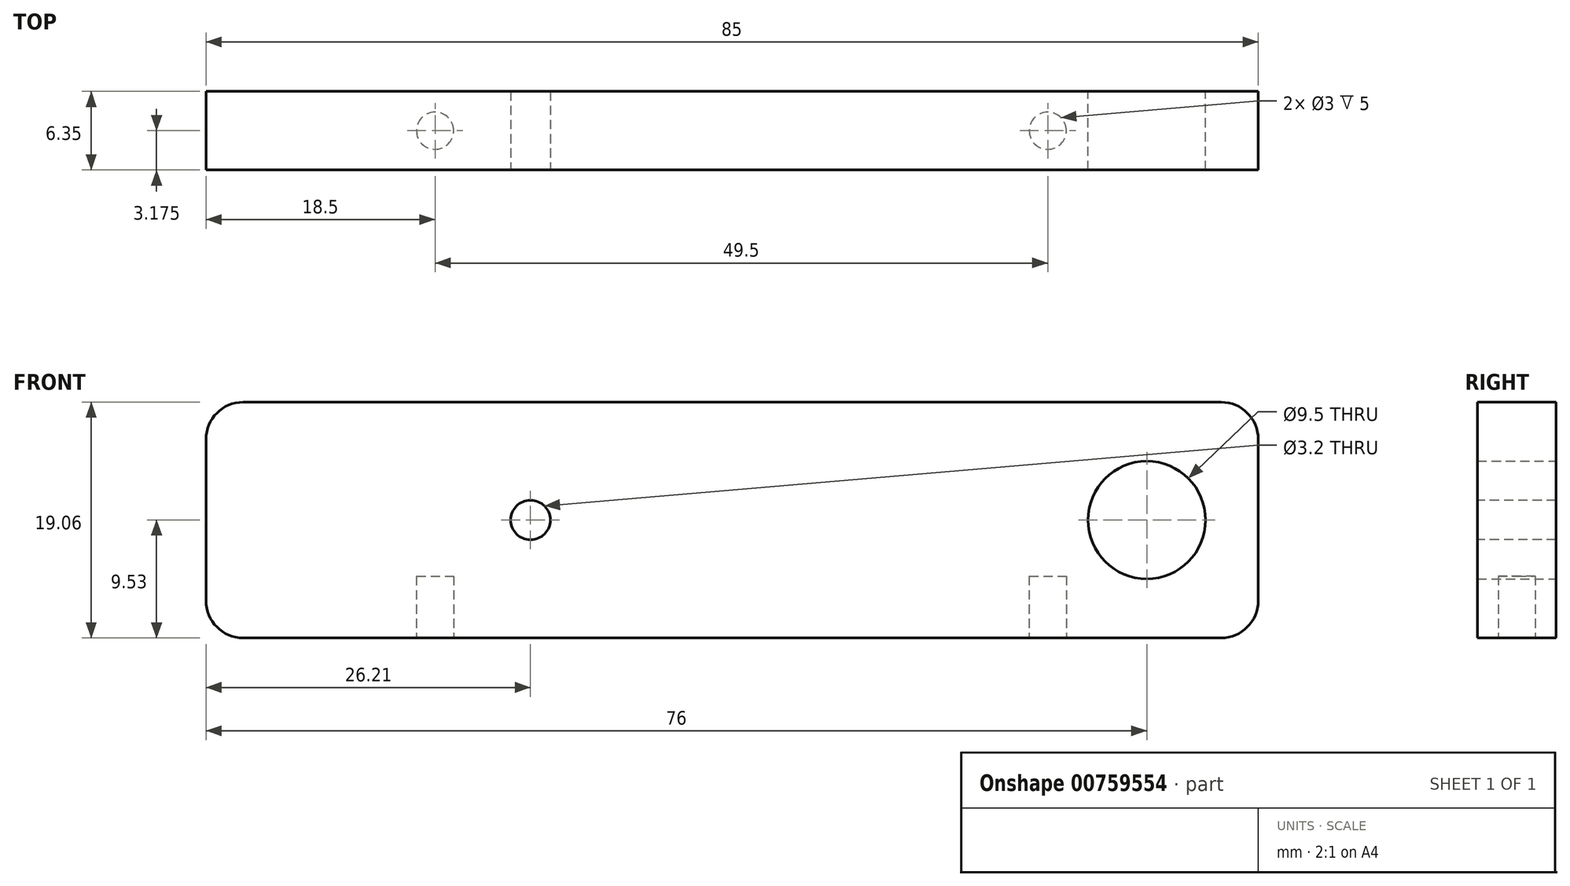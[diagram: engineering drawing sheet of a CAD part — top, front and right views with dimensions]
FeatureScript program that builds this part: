
annotation { "Feature Type Name" : "Feature", "Feature Type Description" : "" }
export const myFeature = defineFeature(function(context is Context, id is Id, definition is map)
    precondition{}
    {
        {
            var Q0;
            Q0=qCreatedBy(makeId("Front.planeOp"),FACE);
            var sketch = newSketch(context, id + "F0", { "sketchPlane" : qUnion([Q0])});
            skLineSegment(sketch, "E0.bottom", {"start": v(42.5, 9.53) * mm, "end": v(-42.5, 9.53) * mm});
            skLineSegment(sketch, "E0.top", {"start": v(42.5, -9.53) * mm, "end": v(-42.5, -9.53) * mm});
            skLineSegment(sketch, "E0.left", {"start": v(42.5, 9.53) * mm, "end": v(42.5, -9.52) * mm});
            skLineSegment(sketch, "E0.right", {"start": v(-42.5, 9.53) * mm, "end": v(-42.5, -9.52) * mm});
            skPoint(sketch, "E0.middle", {"position": v(0, 0) * mm});
            skSolve(sketch);
        }
        {
            var Q0;
            Q0 = qSketchRegion(id + "F0", true);
            extrude(context, id + "F1", {"entities" : qUnion([Q0]), "depth" : 6.35 * mm, "offsetDistance" : 25 * mm});
        }
        {
            var Q0;
            Q0=qCreatedBy(makeId("Front.planeOp"),FACE);
            var sketch = newSketch(context, id + "F2", { "sketchPlane" : qUnion([Q0])});
            skCircle(sketch, "E1", {"center": v(33.5, 0) * mm, "radius": 4.75 * mm});
            skSolve(sketch);
        }
        {
            var Q0;
            Q0 = qSketchRegion(id + "F2", true);
            extrude(context, id + "F3", {"entities" : qUnion([Q0]), "operationType" : NewBodyOperationType.REMOVE, "depth" : 6.35 * mm, "offsetDistance" : 25 * mm});
        }
        {
            var Q0;
            Q0=makeQuery(id+"F1.opExtrude","SWEPT_FACE",FACE,{"disambiguationData":[OSD([sQuery(id+"F0.wireOp",EDGE,"E0.top")])]});
            var sketch = newSketch(context, id + "F4", { "sketchPlane" : qUnion([Q0])});
            skCircle(sketch, "E2", {"center": v(25.5, 3.17) * mm, "radius": 1.5 * mm});
            skPoint(sketch, "E2.centerSnap0", {"position": v(42.5, 3.17) * mm});
            skSolve(sketch);
        }
        {
            var Q0;
            Q0 = qSketchRegion(id + "F4", true);
            extrude(context, id + "F5", {"entities" : qUnion([Q0]), "operationType" : NewBodyOperationType.REMOVE, "oppositeDirection" : true, "depth" : 5 * mm, "offsetDistance" : 25 * mm});
        }
        {
            var Q0;
            Q0=makeQuery(id+"F1.opExtrude","SWEPT_FACE",FACE,{"disambiguationData":[OSD([sQuery(id+"F0.wireOp",EDGE,"E0.top")])]});
            var sketch = newSketch(context, id + "F6", { "sketchPlane" : qUnion([Q0])});
            skCircle(sketch, "E3", {"center": v(-24, 3.18) * mm, "radius": 1.5 * mm});
            skPoint(sketch, "E3.centerSnap0", {"position": v(-42.5, 3.17) * mm});
            skSolve(sketch);
        }
        {
            var Q0;
            Q0 = qSketchRegion(id + "F6", true);
            extrude(context, id + "F7", {"entities" : qUnion([Q0]), "operationType" : NewBodyOperationType.REMOVE, "oppositeDirection" : true, "depth" : 5 * mm, "offsetDistance" : 25 * mm});
        }
        {
            var Q0;
            Q0=makeQuery(id+"F1.opExtrude","CAP_FACE",FACE,{"disambiguationData":[OSD([sQuery(id+"F0.wireOp",EDGE,"E0.bottom"),sQuery(id+"F0.wireOp",EDGE,"E0.top"),sQuery(id+"F0.wireOp",EDGE,"E0.left"),sQuery(id+"F0.wireOp",EDGE,"E0.right")])],"isStart":false});
            var sketch = newSketch(context, id + "F8", { "sketchPlane" : qUnion([Q0])});
            skCircle(sketch, "E4", {"center": v(-16.3, 0) * mm, "radius": 1.6 * mm});
            skPoint(sketch, "E4.centerSnap0", {"position": v(-42.5, 0) * mm});
            skSolve(sketch);
        }
        {
            var Q0;
            Q0 = qSketchRegion(id + "F8", true);
            extrude(context, id + "F9", {"entities" : qUnion([Q0]), "operationType" : NewBodyOperationType.REMOVE, "oppositeDirection" : true, "depth" : 6.35 * mm, "offsetDistance" : 25 * mm});
        }
        {
            var Q0;
            Q0=makeQuery(id+"F1.opExtrude","SWEPT_EDGE",EDGE,{"disambiguationData":[OSD([sQuery(id+"F0.wireOp",EDGE,"E0.bottom"),sQuery(id+"F0.wireOp",EDGE,"E0.right")])]});
            var Q1;
            Q1=makeQuery(id+"F1.opExtrude","SWEPT_EDGE",EDGE,{"disambiguationData":[OSD([sQuery(id+"F0.wireOp",EDGE,"E0.top"),sQuery(id+"F0.wireOp",EDGE,"E0.right")])]});
            var Q2;
            Q2=makeQuery(id+"F1.opExtrude","SWEPT_EDGE",EDGE,{"disambiguationData":[OSD([sQuery(id+"F0.wireOp",EDGE,"E0.bottom"),sQuery(id+"F0.wireOp",EDGE,"E0.left")])]});
            var Q3;
            Q3=makeQuery(id+"F1.opExtrude","SWEPT_EDGE",EDGE,{"disambiguationData":[OSD([sQuery(id+"F0.wireOp",EDGE,"E0.top"),sQuery(id+"F0.wireOp",EDGE,"E0.left")])]});
            fillet(context, id + "F10", {"entities" : qUnion([Q0, Q1, Q2, Q3]), "radius" : 3 * mm, "tangentPropagation" : true, "allowEdgeOverflow" : false});
        }
    });
